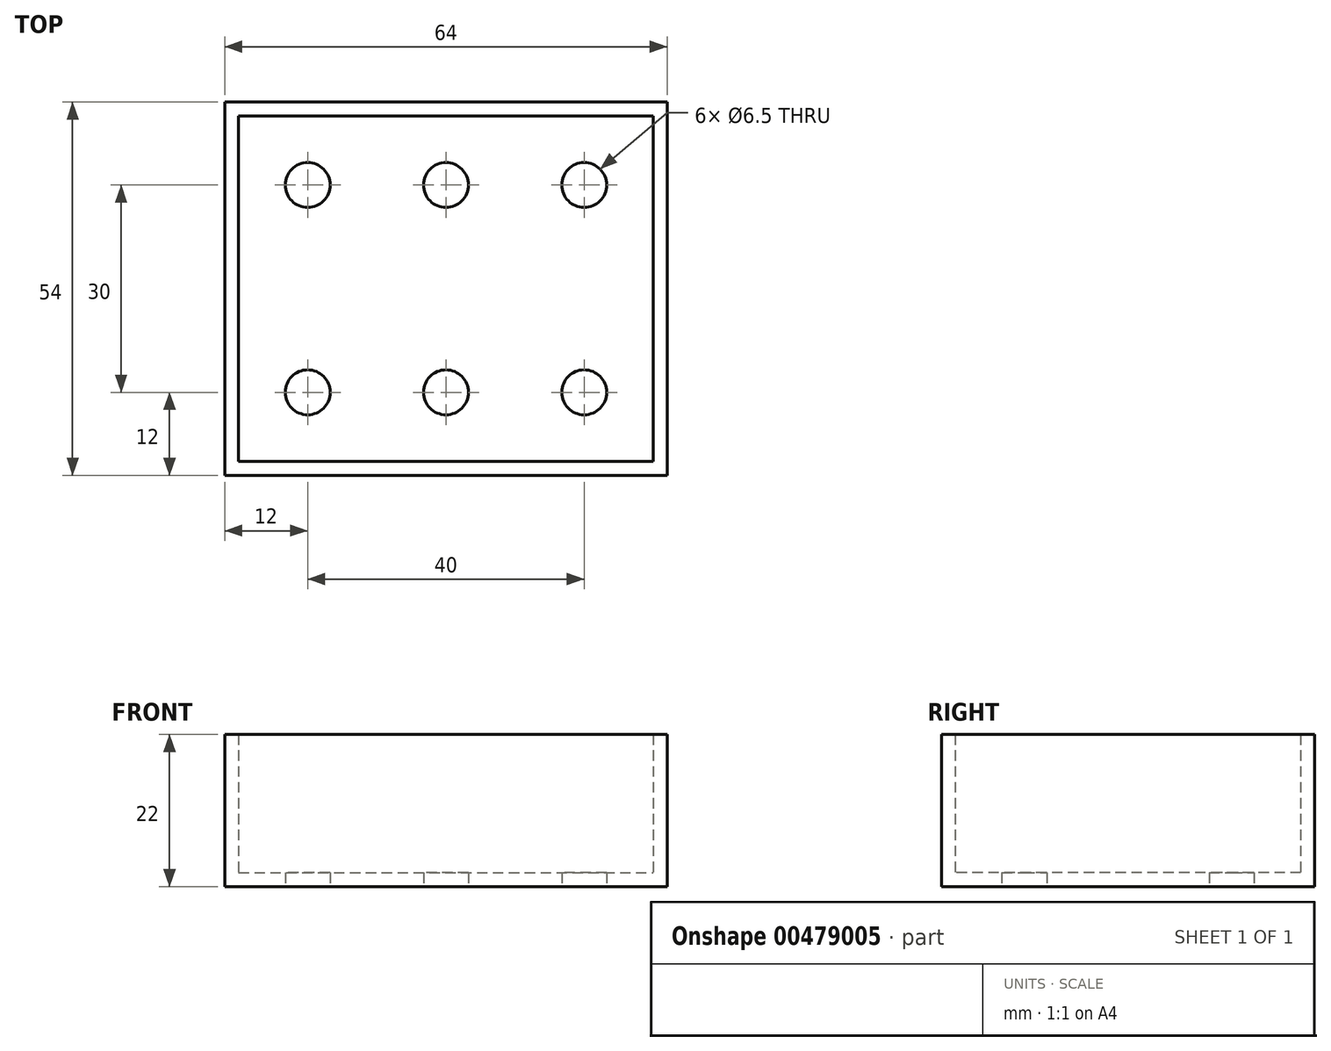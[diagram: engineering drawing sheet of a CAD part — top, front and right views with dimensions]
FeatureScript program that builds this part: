
annotation { "Feature Type Name" : "Feature", "Feature Type Description" : "" }
export const myFeature = defineFeature(function(context is Context, id is Id, definition is map)
    precondition{}
    {
        {
            var Q0;
            Q0=qCreatedBy(makeId("Top.planeOp"),FACE);
            var sketch = newSketch(context, id + "F0", { "sketchPlane" : qUnion([Q0])});
            skLineSegment(sketch, "E0.bottom", {"start": v(30, 25) * mm, "end": v(-30, 25) * mm});
            skLineSegment(sketch, "E0.top", {"start": v(30, -25) * mm, "end": v(-30, -25) * mm});
            skLineSegment(sketch, "E0.left", {"start": v(30, 25) * mm, "end": v(30, -25) * mm});
            skLineSegment(sketch, "E0.right", {"start": v(-30, 25) * mm, "end": v(-30, -25) * mm});
            skPoint(sketch, "E0.middle", {"position": v(0, 0) * mm});
            skCircle(sketch, "E1", {"center": v(-20, -15) * mm, "radius": 3.25 * mm});
            skCircle(sketch, "E2.1.0.0", {"center": v(0, -15) * mm, "radius": 3.25 * mm});
            skCircle(sketch, "E2.2.0.0", {"center": v(20, -15) * mm, "radius": 3.25 * mm});
            skLineSegment(sketch, "E2.direction1", {"start": v(-20, -15) * mm, "end": v(0, -15) * mm, "construction": true});
            skCircle(sketch, "E3.MirrorC", {"center": v(-20, 15) * mm, "radius": 3.25 * mm});
            skCircle(sketch, "E4.MirrorC", {"center": v(0, 15) * mm, "radius": 3.25 * mm});
            skCircle(sketch, "E5.MirrorC", {"center": v(20, 15) * mm, "radius": 3.25 * mm});
            skLineSegment(sketch, "E6.0", {"start": v(32, 27) * mm, "end": v(-32, 27) * mm});
            skLineSegment(sketch, "E6.1", {"start": v(32, 27) * mm, "end": v(32, -27) * mm});
            skLineSegment(sketch, "E6.2", {"start": v(32, -27) * mm, "end": v(-32, -27) * mm});
            skLineSegment(sketch, "E6.3", {"start": v(-32, 27) * mm, "end": v(-32, -27) * mm});
            skSolve(sketch);
        }
        {
            var Q0;
            Q0=makeQuery(id+"F0.imprint","IMPRINT",FACE,{"disambiguationData":[TD([[makeQuery(id+"F0.imprint","IMPRINT",EDGE,{"derivedFrom":sQuery(id+"F0.wireOp",EDGE,"E0.bottom")}),-1.0]])]});
            var Q1;
            Q1=makeQuery(id+"F0.imprint","IMPRINT",FACE,{"disambiguationData":[TD([[makeQuery(id+"F0.imprint","IMPRINT",EDGE,{"derivedFrom":sQuery(id+"F0.wireOp",EDGE,"E0.bottom")}),1.0]])]});
            var Q2;
            Q2=sQuery(id+"F0.wireOp",EDGE,"E0.bottom");
            var Q3;
            Q3=sQuery(id+"F0.wireOp",EDGE,"E0.right");
            var Q4;
            Q4=sQuery(id+"F0.wireOp",EDGE,"E0.top");
            var Q5;
            Q5=sQuery(id+"F0.wireOp",EDGE,"E0.left");
            var Q6;
            Q6=sQuery(id+"F0.wireOp",EDGE,"E2.2.0.0");
            extrude(context, id + "F1", {"entities" : qUnion([Q0, Q1]), "surfaceEntities" : qUnion([Q2, Q3, Q4, Q5, Q6]), "depth" : 2 * mm});
        }
        {
            var Q0;
            Q0=makeQuery(id+"F1.opExtrude","CAP_FACE",FACE,{"disambiguationData":[OSD([sQuery(id+"F0.wireOp",EDGE,"E1"),sQuery(id+"F0.wireOp",EDGE,"E2.1.0.0"),sQuery(id+"F0.wireOp",EDGE,"E2.2.0.0"),sQuery(id+"F0.wireOp",EDGE,"E3.MirrorC"),sQuery(id+"F0.wireOp",EDGE,"E4.MirrorC"),sQuery(id+"F0.wireOp",EDGE,"E5.MirrorC"),sQuery(id+"F0.wireOp",EDGE,"E6.0"),sQuery(id+"F0.wireOp",EDGE,"E6.1"),sQuery(id+"F0.wireOp",EDGE,"E6.2"),sQuery(id+"F0.wireOp",EDGE,"E6.3")])],"isStart":false});
            var sketch = newSketch(context, id + "F2", { "sketchPlane" : qUnion([Q0])});
            skLineSegment(sketch, "E7.bottom", {"start": v(-32, 27) * mm, "end": v(32, 27) * mm});
            skLineSegment(sketch, "E7.top", {"start": v(-32, -27) * mm, "end": v(32, -27) * mm});
            skLineSegment(sketch, "E7.left", {"start": v(-32, 27) * mm, "end": v(-32, -27) * mm});
            skLineSegment(sketch, "E7.right", {"start": v(32, 27) * mm, "end": v(32, -27) * mm});
            skLineSegment(sketch, "E8.0", {"start": v(-30, 25) * mm, "end": v(30, 25) * mm});
            skLineSegment(sketch, "E8.1", {"start": v(-30, 25) * mm, "end": v(-30, -25) * mm});
            skLineSegment(sketch, "E8.2", {"start": v(-30, -25) * mm, "end": v(30, -25) * mm});
            skLineSegment(sketch, "E8.3", {"start": v(30, 25) * mm, "end": v(30, -25) * mm});
            skSolve(sketch);
        }
        {
            var Q0;
            Q0=makeQuery(id+"F2.imprint","IMPRINT",FACE,{"disambiguationData":[TD([[makeQuery(id+"F2.imprint","IMPRINT",EDGE,{"derivedFrom":sQuery(id+"F2.wireOp",EDGE,"E7.bottom")}),1.0]])]});
            extrude(context, id + "F3", {"entities" : qUnion([Q0]), "operationType" : NewBodyOperationType.ADD, "depth" : 20 * mm});
        }
    });
